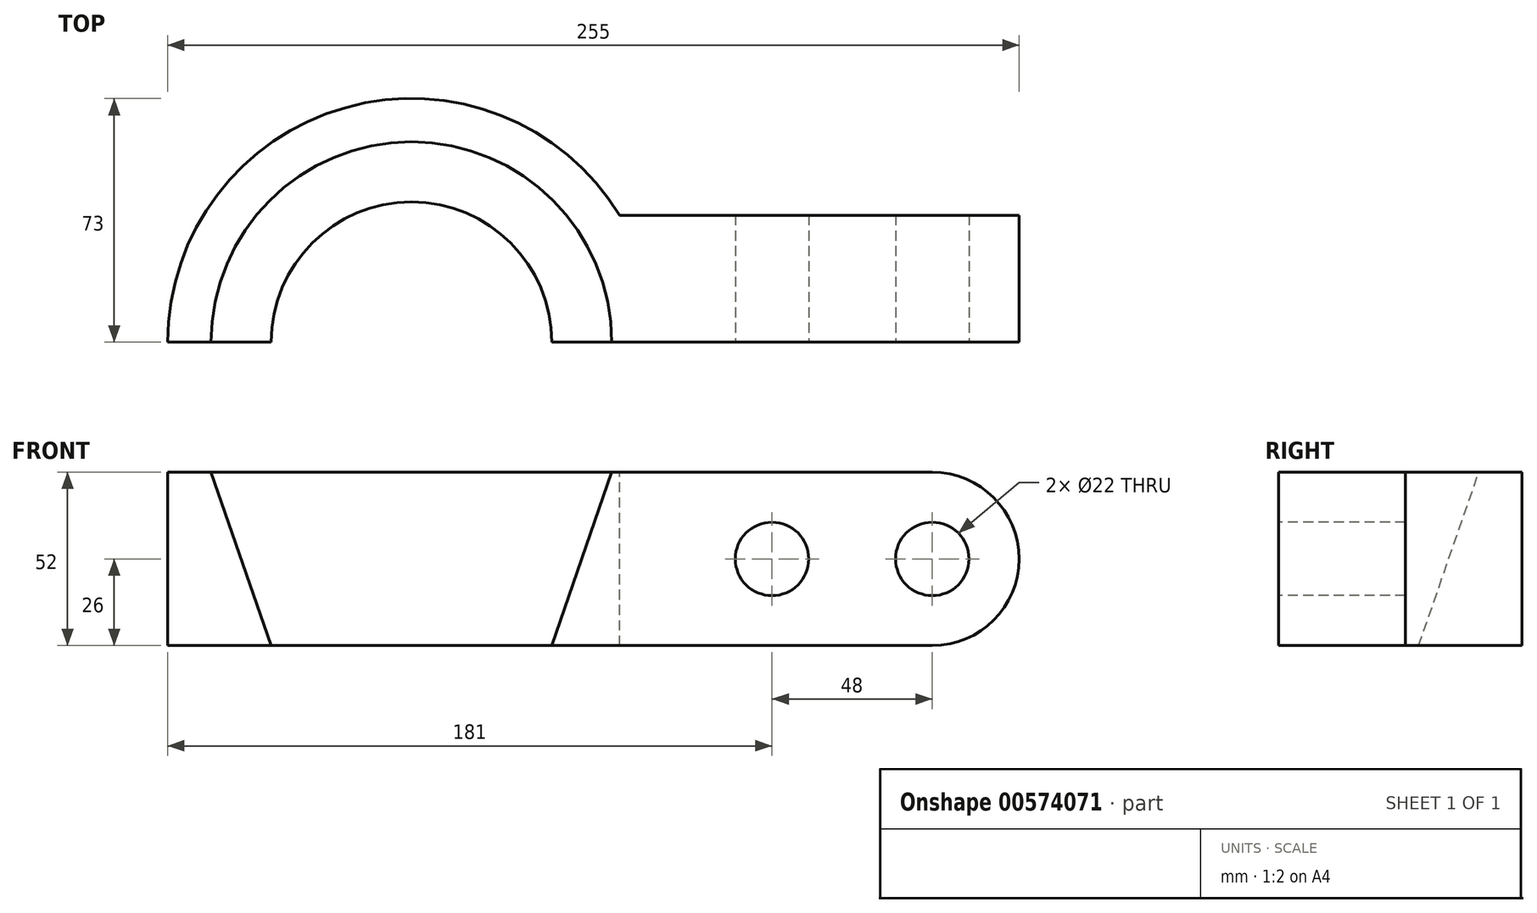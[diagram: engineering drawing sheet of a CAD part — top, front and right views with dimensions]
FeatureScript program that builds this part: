
annotation { "Feature Type Name" : "Feature", "Feature Type Description" : "" }
export const myFeature = defineFeature(function(context is Context, id is Id, definition is map)
    precondition{}
    {
        {
            var Q0;
            Q0=qCreatedBy(makeId("Front.planeOp"),FACE);
            var sketch = newSketch(context, id + "F0", { "sketchPlane" : qUnion([Q0])});
            skLineSegment(sketch, "E0", {"start": v(-73, 52) * mm, "end": v(-60, 52) * mm});
            skLineSegment(sketch, "E1", {"start": v(-60, 52) * mm, "end": v(-42, 0) * mm});
            skLineSegment(sketch, "E2", {"start": v(-42, 0) * mm, "end": v(-73, 0) * mm});
            skLineSegment(sketch, "E3", {"start": v(-73, 0) * mm, "end": v(-73, 52) * mm});
            skLineSegment(sketch, "E4", {"start": v(0, 66.24) * mm, "end": v(0, -17.58) * mm, "construction": true});
            skSolve(sketch);
        }
        {
            var Q0;
            Q0 = qSketchRegion(id + "F0", true);
            var Q1;
            Q1=sQuery(id+"F0.wireOp",EDGE,"E4");
            revolve(context, id + "F1", {"entities" : qUnion([Q0]), "axis" : qUnion([Q1]), "revolveType" : RevolveType.ONE_DIRECTION, "angle" : 180 * degree});
        }
        {
            var Q0;
            Q0=qCreatedBy(makeId("Front.planeOp"),FACE);
            var sketch = newSketch(context, id + "F2", { "sketchPlane" : qUnion([Q0])});
            skLineSegment(sketch, "E5.0.0", {"start": v(73, 0) * mm, "end": v(73, 52) * mm, "construction": true});
            skLineSegment(sketch, "E5.0.1", {"start": v(73, 52) * mm, "end": v(60, 52) * mm, "construction": true});
            skLineSegment(sketch, "E5.0.2", {"start": v(60, 52) * mm, "end": v(42, 0) * mm, "construction": true});
            skLineSegment(sketch, "E5.0.3", {"start": v(42, 0) * mm, "end": v(73, 0) * mm, "construction": true});
            skLineSegment(sketch, "E6.bottom", {"start": v(60, 52) * mm, "end": v(156, 52) * mm});
            skLineSegment(sketch, "E6.top", {"start": v(60, 0) * mm, "end": v(156, 0) * mm});
            skLineSegment(sketch, "E6.left", {"start": v(60, 52) * mm, "end": v(60, 0) * mm});
            skLineSegment(sketch, "E6.right", {"start": v(182, 26) * mm, "end": v(182, 26) * mm});
            skPoint(sketch, "E7.visualSharp", {"position": v(182, 52) * mm});
            skArc(sketch, "E7.filletArc", {"start": v(182, 26) * mm, "mid": v(174.38, 44.38) * mm, "end": v(156, 52) * mm});
            skPoint(sketch, "E8.visualSharp", {"position": v(182, 0) * mm});
            skArc(sketch, "E8.filletArc", {"start": v(156, 0) * mm, "mid": v(174.38, 7.62) * mm, "end": v(182, 26) * mm});
            skCircle(sketch, "E9", {"center": v(156, 26) * mm, "radius": 11 * mm});
            skCircle(sketch, "E10", {"center": v(108, 26) * mm, "radius": 11 * mm});
            skSolve(sketch);
        }
        {
            var Q0;
            Q0 = qSketchRegion(id + "F2", true);
            extrude(context, id + "F3", {"entities" : qUnion([Q0]), "operationType" : NewBodyOperationType.ADD, "oppositeDirection" : true, "depth" : 38 * mm, "offsetDistance" : 25 * mm});
        }
    });
